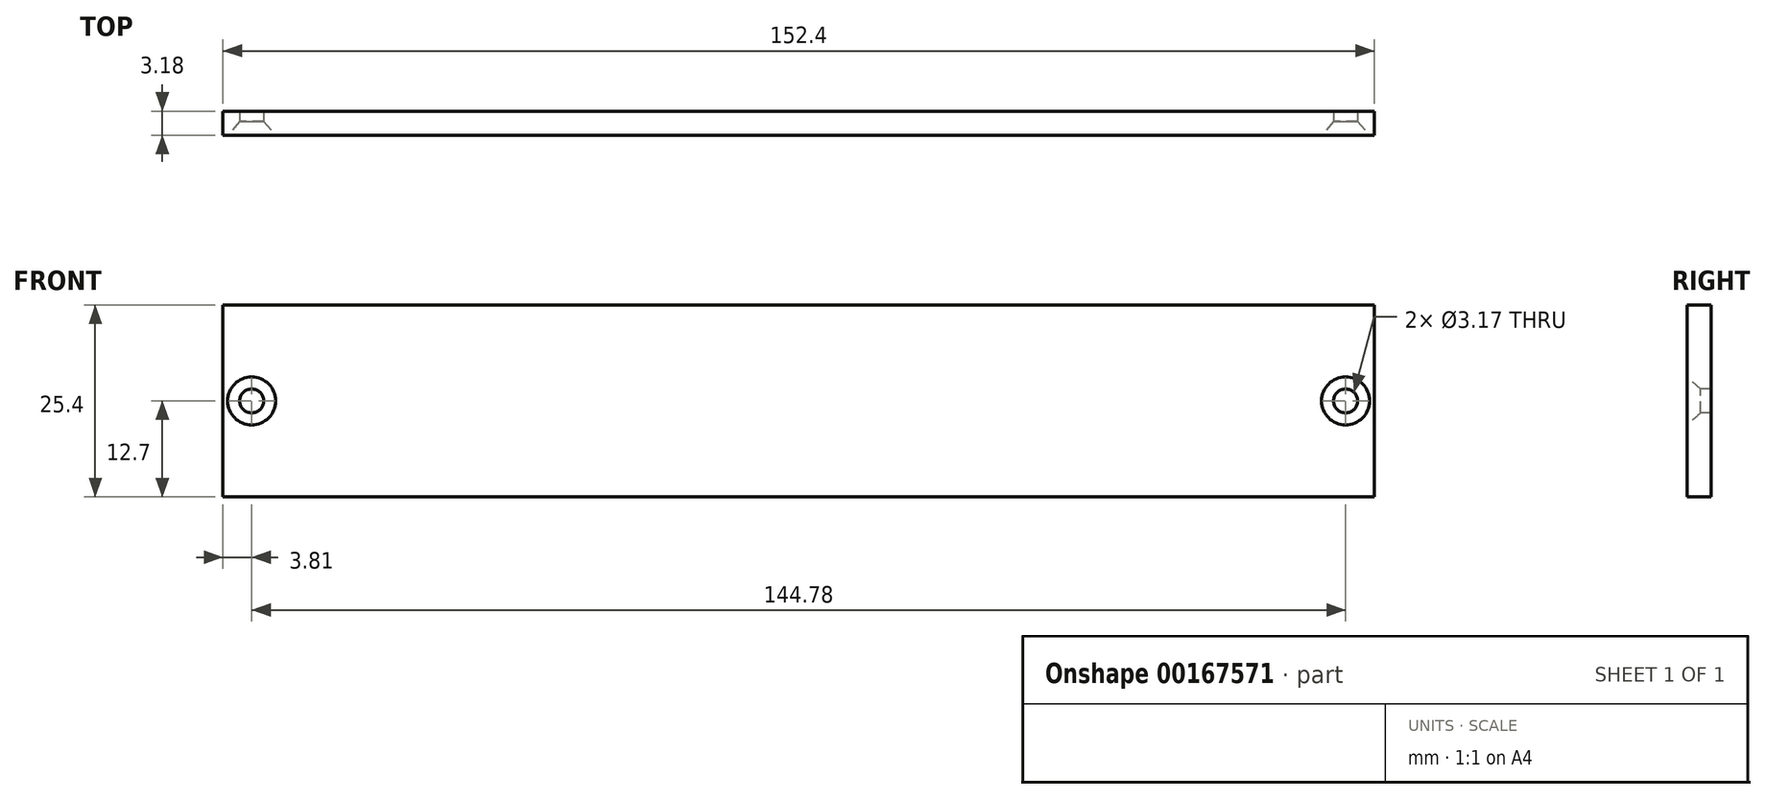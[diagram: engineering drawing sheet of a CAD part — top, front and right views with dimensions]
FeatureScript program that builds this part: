
annotation { "Feature Type Name" : "Feature", "Feature Type Description" : "" }
export const myFeature = defineFeature(function(context is Context, id is Id, definition is map)
    precondition{}
    {
        {
            var Q0;
            Q0=qCreatedBy(makeId("Front.planeOp"),FACE);
            var sketch = newSketch(context, id + "F0", { "sketchPlane" : qUnion([Q0])});
            skLineSegment(sketch, "E0.bottom", {"start": v(0, 0) * mm, "end": v(152.4, 0) * mm});
            skLineSegment(sketch, "E0.top", {"start": v(0, 25.4) * mm, "end": v(152.4, 25.4) * mm});
            skLineSegment(sketch, "E0.left", {"start": v(0, 0) * mm, "end": v(0, 25.4) * mm});
            skLineSegment(sketch, "E0.right", {"start": v(152.4, 0) * mm, "end": v(152.4, 25.4) * mm});
            skSolve(sketch);
        }
        {
            var Q0;
            Q0=qSketchRegion(id+"F0",true);
            extrude(context, id + "F1", {"entities" : qUnion([Q0]), "depth" : 3.17 * mm});
        }
        {
            var Q0;
            Q0=makeQuery(id+"F1.opExtrude","CAP_FACE",FACE,{"disambiguationData":[OSD([sQuery(id+"F0.wireOp",EDGE,"E0.bottom"),sQuery(id+"F0.wireOp",EDGE,"E0.top"),sQuery(id+"F0.wireOp",EDGE,"E0.left"),sQuery(id+"F0.wireOp",EDGE,"E0.right")])],"isStart":false});
            var sketch = newSketch(context, id + "F2", { "sketchPlane" : qUnion([Q0])});
            skPoint(sketch, "E1", {"position": v(3.81, 12.7) * mm});
            skPoint(sketch, "E1.positionSnap0", {"position": v(0, 12.7) * mm});
            skPoint(sketch, "E2", {"position": v(152.4, 12.7) * mm});
            skPoint(sketch, "E3", {"position": v(148.6, 12.7) * mm});
            skSolve(sketch);
        }
        {
            var Q0;
            Q0=sQuery(id+"F2.wireOp",VERTEX,"E1");
            var Q1;
            Q1=sQuery(id+"F2.wireOp",VERTEX,"E3");
            var Q2;
            Q2=makeQuery(id+"F1.opExtrude","SWEPT_BODY",BODY,{"disambiguationData":[OSD([sQuery(id+"F0.wireOp",EDGE,"E0.bottom"),sQuery(id+"F0.wireOp",EDGE,"E0.top"),sQuery(id+"F0.wireOp",EDGE,"E0.left"),sQuery(id+"F0.wireOp",EDGE,"E0.right")])]});
            hole(context, id + "F3", {"style" : HoleStyle.C_SINK, "endStyle" : HoleEndStyle.THROUGH, "holeDiameter" : 3.17 * mm, "cSinkDiameter" : 6.35 * mm, "cSinkAngle" : 82 * degree, "locations" : qUnion([Q0, Q1]), "scope" : qUnion([Q2]), "isTappedThrough" : true});
        }
    });
